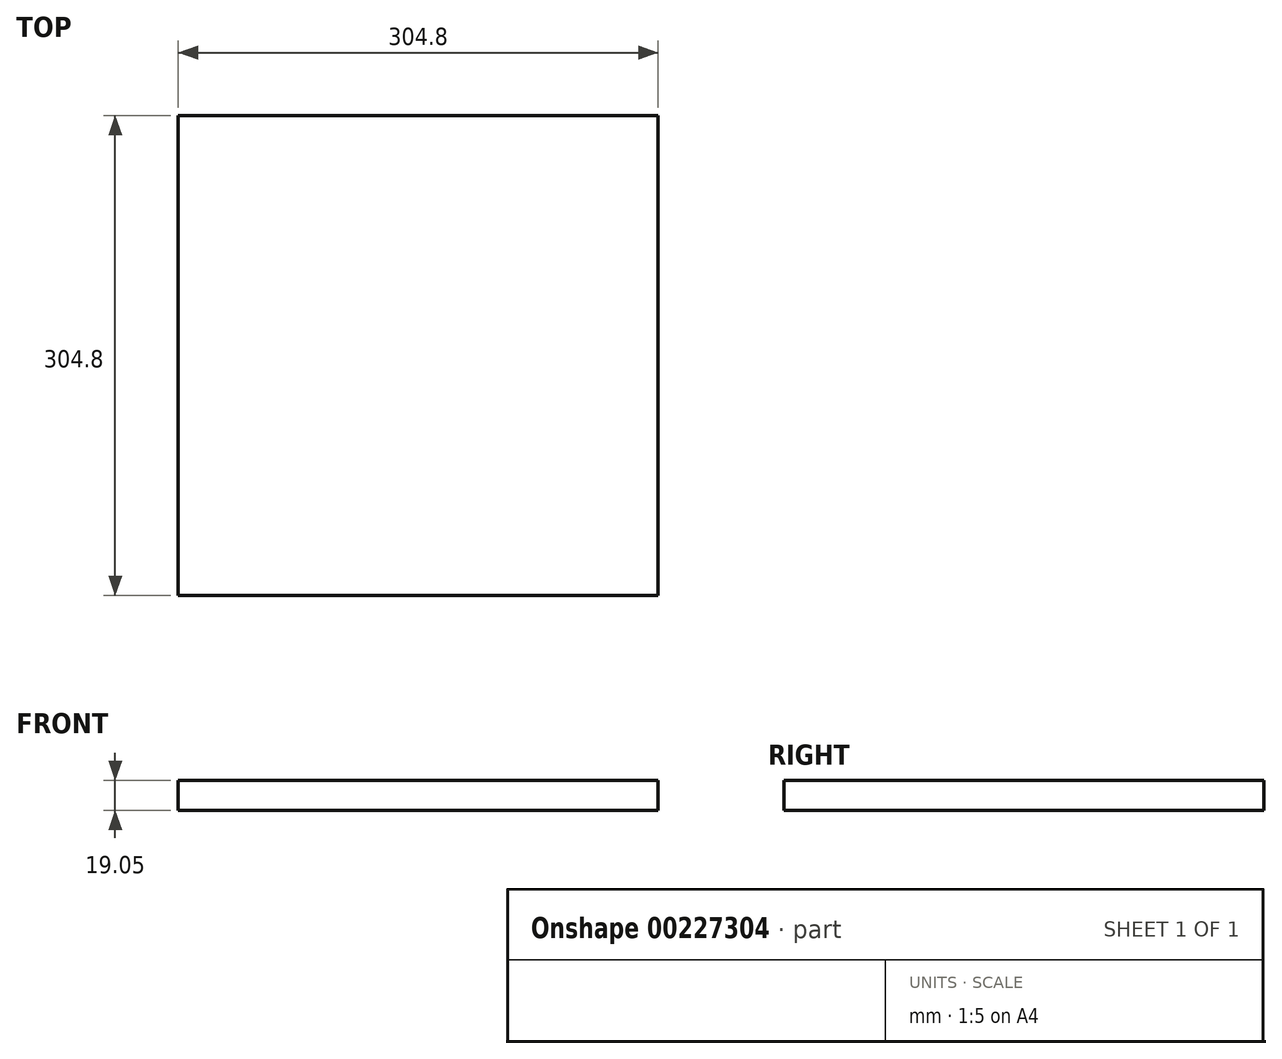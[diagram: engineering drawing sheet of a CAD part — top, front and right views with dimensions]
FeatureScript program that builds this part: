
annotation { "Feature Type Name" : "Feature", "Feature Type Description" : "" }
export const myFeature = defineFeature(function(context is Context, id is Id, definition is map)
    precondition{}
    {
        {
            var Q0;
            Q0=qCreatedBy(makeId("Top.planeOp"),FACE);
            var sketch = newSketch(context, id + "F0", { "sketchPlane" : qUnion([Q0])});
            skLineSegment(sketch, "E0.bottom", {"start": v(-154.33, 157.06) * mm, "end": v(150.47, 157.06) * mm});
            skLineSegment(sketch, "E0.top", {"start": v(-154.33, -147.74) * mm, "end": v(150.47, -147.74) * mm});
            skLineSegment(sketch, "E0.left", {"start": v(-154.33, 157.06) * mm, "end": v(-154.33, -147.74) * mm});
            skLineSegment(sketch, "E0.right", {"start": v(150.47, 157.06) * mm, "end": v(150.47, -147.74) * mm});
            skSolve(sketch);
        }
        {
            var Q0;
            Q0 = qSketchRegion(id + "F0", true);
            extrude(context, id + "F1", {"entities" : qUnion([Q0]), "depth" : 19.05 * mm});
        }
    });
